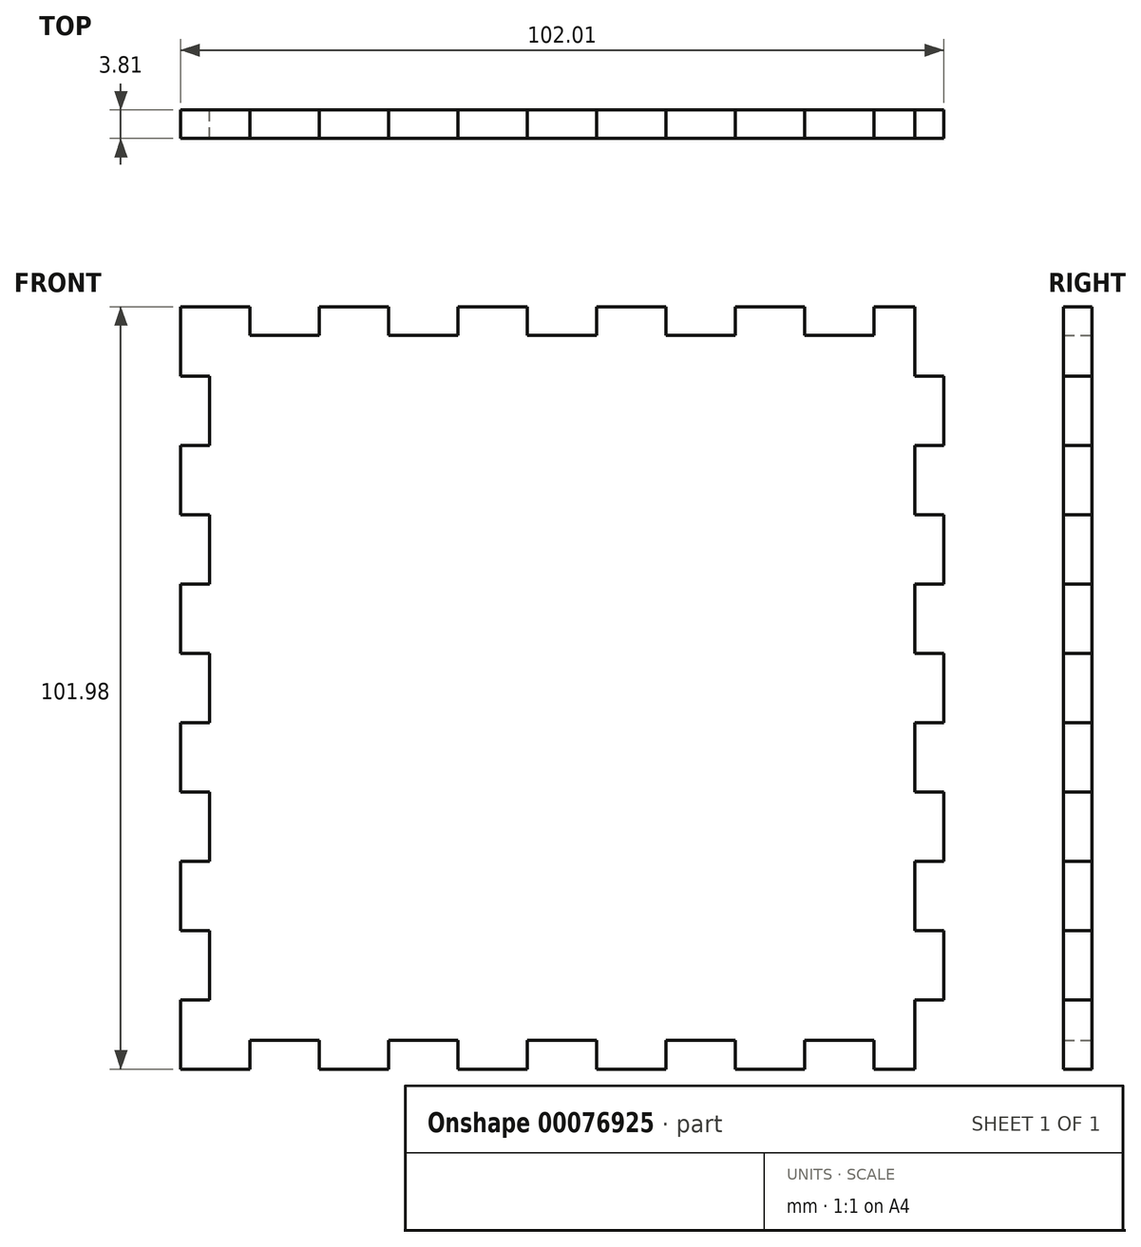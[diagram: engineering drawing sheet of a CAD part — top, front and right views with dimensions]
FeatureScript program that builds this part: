
annotation { "Feature Type Name" : "Feature", "Feature Type Description" : "" }
export const myFeature = defineFeature(function(context is Context, id is Id, definition is map)
    precondition{}
    {
        {
            var Q0;
            Q0=qCreatedBy(makeId("Front.planeOp"),FACE);
            var sketch = newSketch(context, id + "F0", { "sketchPlane" : qUnion([Q0])});
            skLineSegment(sketch, "E0", {"start": v(-55.63, 61.06) * mm, "end": v(-55.63, 51.8) * mm});
            skLineSegment(sketch, "E1", {"start": v(-55.63, 61.06) * mm, "end": v(-46.36, 61.06) * mm});
            skLineSegment(sketch, "E2", {"start": v(-46.36, 61.06) * mm, "end": v(-46.36, 57.23) * mm});
            skLineSegment(sketch, "E3", {"start": v(-46.36, 57.23) * mm, "end": v(-37.08, 57.23) * mm});
            skLineSegment(sketch, "E4", {"start": v(-37.08, 57.23) * mm, "end": v(-37.08, 61.06) * mm});
            skLineSegment(sketch, "E5", {"start": v(-37.08, 61.06) * mm, "end": v(-27.81, 61.06) * mm});
            skLineSegment(sketch, "E6", {"start": v(-27.81, 61.06) * mm, "end": v(-27.81, 57.23) * mm});
            skLineSegment(sketch, "E7", {"start": v(-27.81, 57.23) * mm, "end": v(-18.54, 57.23) * mm});
            skLineSegment(sketch, "E8", {"start": v(-18.54, 57.23) * mm, "end": v(-18.54, 61.06) * mm});
            skLineSegment(sketch, "E9", {"start": v(-18.54, 61.06) * mm, "end": v(-9.27, 61.06) * mm});
            skLineSegment(sketch, "E10", {"start": v(-9.27, 61.06) * mm, "end": v(-9.27, 57.23) * mm});
            skLineSegment(sketch, "E11", {"start": v(-9.27, 57.23) * mm, "end": v(0, 57.23) * mm});
            skLineSegment(sketch, "E12", {"start": v(0, 57.23) * mm, "end": v(0, 61.06) * mm});
            skLineSegment(sketch, "E13", {"start": v(0, 61.06) * mm, "end": v(9.27, 61.06) * mm});
            skLineSegment(sketch, "E14", {"start": v(9.27, 61.06) * mm, "end": v(9.27, 57.23) * mm});
            skLineSegment(sketch, "E15", {"start": v(9.27, 57.23) * mm, "end": v(18.54, 57.23) * mm});
            skLineSegment(sketch, "E16", {"start": v(18.54, 57.23) * mm, "end": v(18.54, 61.06) * mm});
            skLineSegment(sketch, "E17", {"start": v(18.54, 61.06) * mm, "end": v(27.81, 61.06) * mm});
            skLineSegment(sketch, "E18", {"start": v(27.81, 61.06) * mm, "end": v(27.81, 57.23) * mm});
            skLineSegment(sketch, "E19", {"start": v(27.81, 57.23) * mm, "end": v(37.08, 57.23) * mm});
            skLineSegment(sketch, "E20", {"start": v(37.08, 57.23) * mm, "end": v(37.08, 61.06) * mm});
            skLineSegment(sketch, "E21", {"start": v(37.08, 61.06) * mm, "end": v(42.55, 61.06) * mm});
            skLineSegment(sketch, "E22", {"start": v(42.55, 61.06) * mm, "end": v(42.55, 51.8) * mm});
            skLineSegment(sketch, "E23", {"start": v(42.55, 51.8) * mm, "end": v(46.38, 51.8) * mm});
            skLineSegment(sketch, "E24", {"start": v(46.38, 51.8) * mm, "end": v(46.38, 42.52) * mm});
            skLineSegment(sketch, "E25", {"start": v(46.38, 42.52) * mm, "end": v(42.55, 42.52) * mm});
            skLineSegment(sketch, "E26", {"start": v(42.55, 42.52) * mm, "end": v(42.55, 33.25) * mm});
            skLineSegment(sketch, "E27", {"start": v(42.55, 33.25) * mm, "end": v(46.38, 33.25) * mm});
            skLineSegment(sketch, "E28", {"start": v(46.38, 33.25) * mm, "end": v(46.38, 23.98) * mm});
            skLineSegment(sketch, "E29", {"start": v(46.38, 23.98) * mm, "end": v(42.55, 23.98) * mm});
            skLineSegment(sketch, "E30", {"start": v(42.55, 23.98) * mm, "end": v(42.55, 14.7) * mm});
            skLineSegment(sketch, "E31", {"start": v(42.55, 14.7) * mm, "end": v(46.38, 14.7) * mm});
            skLineSegment(sketch, "E32", {"start": v(46.38, 14.7) * mm, "end": v(46.38, 5.44) * mm});
            skLineSegment(sketch, "E33", {"start": v(46.38, 5.44) * mm, "end": v(42.55, 5.44) * mm});
            skLineSegment(sketch, "E34", {"start": v(42.55, 5.44) * mm, "end": v(42.55, -3.84) * mm});
            skLineSegment(sketch, "E35", {"start": v(42.55, -3.84) * mm, "end": v(46.38, -3.84) * mm});
            skLineSegment(sketch, "E36", {"start": v(46.38, -3.84) * mm, "end": v(46.38, -13.1) * mm});
            skLineSegment(sketch, "E37", {"start": v(46.38, -13.1) * mm, "end": v(42.55, -13.1) * mm});
            skLineSegment(sketch, "E38", {"start": v(42.55, -13.1) * mm, "end": v(42.55, -22.38) * mm});
            skLineSegment(sketch, "E39", {"start": v(42.55, -22.38) * mm, "end": v(46.38, -22.38) * mm});
            skPoint(sketch, "E39.endSnap0", {"position": v(46.38, -8.47) * mm});
            skLineSegment(sketch, "E40", {"start": v(46.38, -22.38) * mm, "end": v(46.38, -31.65) * mm});
            skLineSegment(sketch, "E41", {"start": v(46.38, -31.65) * mm, "end": v(42.55, -31.65) * mm});
            skLineSegment(sketch, "E42", {"start": v(42.55, -31.65) * mm, "end": v(42.55, -40.92) * mm});
            skLineSegment(sketch, "E43", {"start": v(42.55, -40.92) * mm, "end": v(37.08, -40.92) * mm});
            skLineSegment(sketch, "E44", {"start": v(37.08, -40.92) * mm, "end": v(37.08, -37.08) * mm});
            skLineSegment(sketch, "E45", {"start": v(37.08, -37.08) * mm, "end": v(27.81, -37.08) * mm});
            skLineSegment(sketch, "E46", {"start": v(27.81, -37.08) * mm, "end": v(27.81, -40.92) * mm});
            skLineSegment(sketch, "E47", {"start": v(27.81, -40.92) * mm, "end": v(18.54, -40.92) * mm});
            skLineSegment(sketch, "E48", {"start": v(18.54, -40.92) * mm, "end": v(18.54, -37.08) * mm});
            skLineSegment(sketch, "E49", {"start": v(18.54, -37.08) * mm, "end": v(9.27, -37.08) * mm});
            skLineSegment(sketch, "E50", {"start": v(9.27, -37.08) * mm, "end": v(9.27, -40.92) * mm});
            skLineSegment(sketch, "E51", {"start": v(9.27, -40.92) * mm, "end": v(0, -40.92) * mm});
            skLineSegment(sketch, "E52", {"start": v(0, -40.92) * mm, "end": v(0, -37.08) * mm});
            skLineSegment(sketch, "E53", {"start": v(0, -37.08) * mm, "end": v(-9.27, -37.08) * mm});
            skLineSegment(sketch, "E54", {"start": v(-9.27, -37.08) * mm, "end": v(-9.27, -40.92) * mm});
            skLineSegment(sketch, "E55", {"start": v(-9.27, -40.92) * mm, "end": v(-18.54, -40.92) * mm});
            skLineSegment(sketch, "E56", {"start": v(-18.54, -40.92) * mm, "end": v(-18.54, -37.08) * mm});
            skLineSegment(sketch, "E57", {"start": v(-18.54, -37.08) * mm, "end": v(-27.81, -37.08) * mm});
            skLineSegment(sketch, "E58", {"start": v(-27.81, -37.08) * mm, "end": v(-27.81, -40.92) * mm});
            skLineSegment(sketch, "E59", {"start": v(-27.81, -40.92) * mm, "end": v(-37.08, -40.92) * mm});
            skLineSegment(sketch, "E60", {"start": v(-37.08, -40.92) * mm, "end": v(-37.08, -37.08) * mm});
            skLineSegment(sketch, "E61", {"start": v(-37.08, -37.08) * mm, "end": v(-46.35, -37.08) * mm});
            skLineSegment(sketch, "E62", {"start": v(-46.35, -37.08) * mm, "end": v(-46.35, -40.92) * mm});
            skLineSegment(sketch, "E63", {"start": v(-46.35, -40.92) * mm, "end": v(-55.63, -40.92) * mm});
            skLineSegment(sketch, "E64", {"start": v(-55.63, -40.92) * mm, "end": v(-55.63, -31.65) * mm});
            skLineSegment(sketch, "E65", {"start": v(-55.63, -31.65) * mm, "end": v(-51.8, -31.65) * mm});
            skLineSegment(sketch, "E66", {"start": v(-51.8, -31.65) * mm, "end": v(-51.8, -22.38) * mm});
            skLineSegment(sketch, "E67", {"start": v(-51.8, -22.38) * mm, "end": v(-55.63, -22.38) * mm});
            skLineSegment(sketch, "E68", {"start": v(-55.63, -22.38) * mm, "end": v(-55.63, -13.1) * mm});
            skLineSegment(sketch, "E69", {"start": v(-55.63, -13.1) * mm, "end": v(-51.8, -13.1) * mm});
            skLineSegment(sketch, "E70", {"start": v(-51.8, -13.1) * mm, "end": v(-51.8, -3.84) * mm});
            skLineSegment(sketch, "E71", {"start": v(-51.8, -3.84) * mm, "end": v(-55.63, -3.84) * mm});
            skLineSegment(sketch, "E72", {"start": v(-55.63, -3.84) * mm, "end": v(-55.63, 5.44) * mm});
            skLineSegment(sketch, "E73", {"start": v(-55.63, 5.44) * mm, "end": v(-51.8, 5.44) * mm});
            skLineSegment(sketch, "E74", {"start": v(-51.8, 5.44) * mm, "end": v(-51.8, 14.7) * mm});
            skLineSegment(sketch, "E75", {"start": v(-51.8, 14.7) * mm, "end": v(-55.63, 14.7) * mm});
            skLineSegment(sketch, "E76", {"start": v(-55.63, 14.7) * mm, "end": v(-55.63, 23.98) * mm});
            skLineSegment(sketch, "E77", {"start": v(-55.63, 23.98) * mm, "end": v(-51.8, 23.98) * mm});
            skLineSegment(sketch, "E78", {"start": v(-51.8, 23.98) * mm, "end": v(-51.8, 33.25) * mm});
            skLineSegment(sketch, "E79", {"start": v(-55.63, 33.25) * mm, "end": v(-51.8, 33.25) * mm});
            skLineSegment(sketch, "E80", {"start": v(-55.63, 33.25) * mm, "end": v(-55.63, 42.52) * mm});
            skLineSegment(sketch, "E81", {"start": v(-55.63, 42.52) * mm, "end": v(-51.8, 42.52) * mm});
            skLineSegment(sketch, "E82", {"start": v(-51.8, 42.52) * mm, "end": v(-51.8, 51.8) * mm});
            skLineSegment(sketch, "E83", {"start": v(-51.8, 51.8) * mm, "end": v(-55.63, 51.8) * mm});
            skSolve(sketch);
        }
        {
            var Q0;
            Q0=makeQuery(id+"F0.imprint","IMPRINT",FACE,{"disambiguationData":[TD([[makeQuery(id+"F0.imprint","IMPRINT",EDGE,{"derivedFrom":sQuery(id+"F0.wireOp",EDGE,"E0")}),1.0]])]});
            extrude(context, id + "F1", {"entities" : qUnion([Q0]), "depth" : 3.8 * mm});
        }
    });
